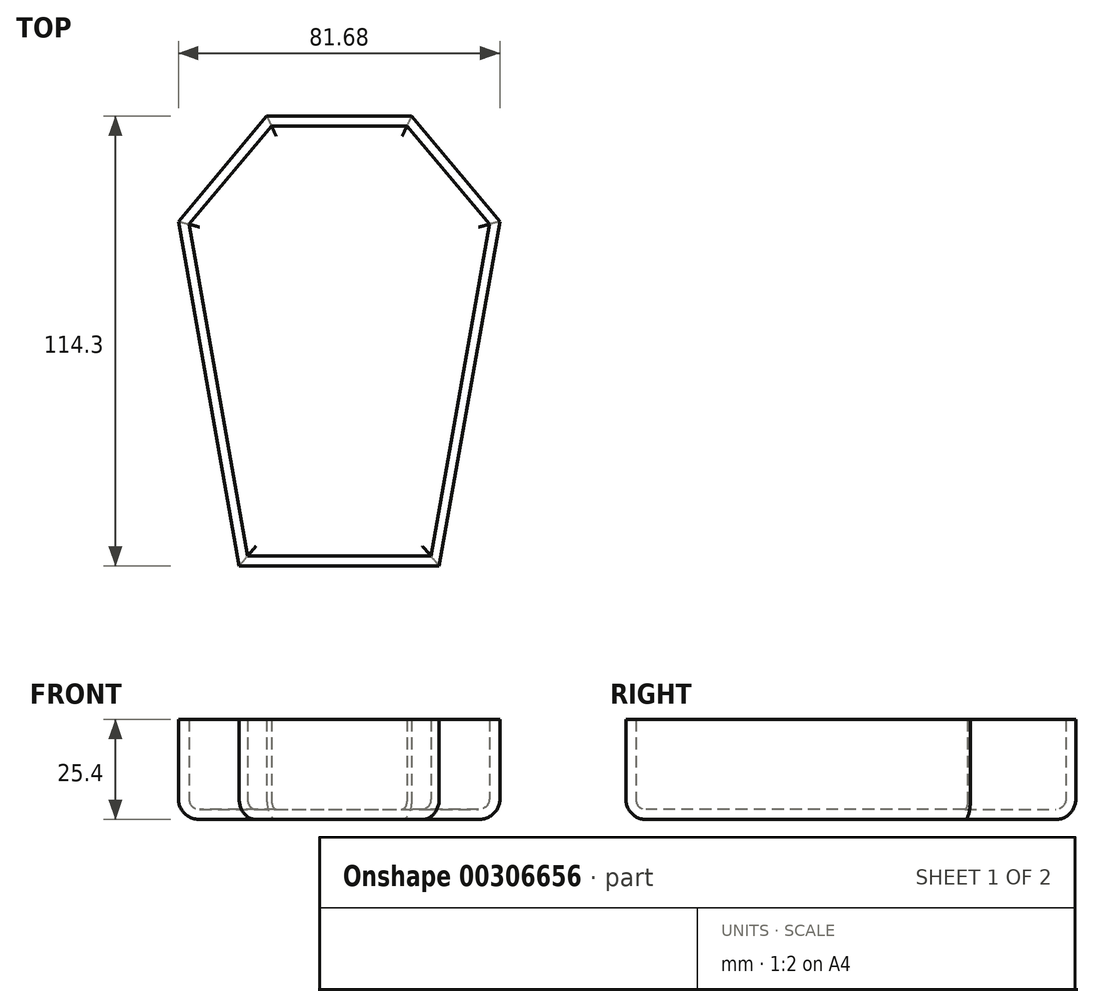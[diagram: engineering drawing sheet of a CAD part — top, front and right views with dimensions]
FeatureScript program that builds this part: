
annotation { "Feature Type Name" : "Feature", "Feature Type Description" : "" }
export const myFeature = defineFeature(function(context is Context, id is Id, definition is map)
    precondition{}
    {
        {
            var Q0;
            Q0=qCreatedBy(makeId("Top.planeOp"),FACE);
            var sketch = newSketch(context, id + "F0", { "sketchPlane" : qUnion([Q0])});
            skLineSegment(sketch, "E0", {"start": v(-35.6, 28) * mm, "end": v(-20.17, -59.55) * mm});
            skLineSegment(sketch, "E1", {"start": v(-20.17, -59.55) * mm, "end": v(30.63, -59.55) * mm});
            skLineSegment(sketch, "E2", {"start": v(30.63, -59.55) * mm, "end": v(46.07, 28) * mm});
            skLineSegment(sketch, "E3", {"start": v(46.07, 28) * mm, "end": v(23.62, 54.75) * mm});
            skLineSegment(sketch, "E4", {"start": v(23.62, 54.75) * mm, "end": v(-13.16, 54.75) * mm});
            skLineSegment(sketch, "E5", {"start": v(-13.16, 54.75) * mm, "end": v(-35.6, 28) * mm});
            skSolve(sketch);
        }
        {
            var Q0;
            Q0=makeQuery(id+"F0.imprint","IMPRINT",FACE,{"disambiguationData":[TD([[makeQuery(id+"F0.imprint","IMPRINT",EDGE,{"derivedFrom":sQuery(id+"F0.wireOp",EDGE,"E0")}),1.0]])]});
            extrude(context, id + "F1", {"entities" : qUnion([Q0]), "depth" : 25.4 * mm});
        }
        {
            var Q0;
            Q0=makeQuery(id+"F1.opExtrude","CAP_EDGE",EDGE,{"disambiguationData":[OSD([sQuery(id+"F0.wireOp",EDGE,"E0")])],"isStart":true});
            var Q1;
            Q1=makeQuery(id+"F1.opExtrude","CAP_EDGE",EDGE,{"disambiguationData":[OSD([sQuery(id+"F0.wireOp",EDGE,"E1")])],"isStart":true});
            var Q2;
            Q2=makeQuery(id+"F1.opExtrude","CAP_EDGE",EDGE,{"disambiguationData":[OSD([sQuery(id+"F0.wireOp",EDGE,"E2")])],"isStart":true});
            var Q3;
            Q3=makeQuery(id+"F1.opExtrude","CAP_EDGE",EDGE,{"disambiguationData":[OSD([sQuery(id+"F0.wireOp",EDGE,"E3")])],"isStart":true});
            var Q4;
            Q4=makeQuery(id+"F1.opExtrude","CAP_EDGE",EDGE,{"disambiguationData":[OSD([sQuery(id+"F0.wireOp",EDGE,"E4")])],"isStart":true});
            var Q5;
            Q5=makeQuery(id+"F1.opExtrude","CAP_EDGE",EDGE,{"disambiguationData":[OSD([sQuery(id+"F0.wireOp",EDGE,"E5")])],"isStart":true});
            fillet(context, id + "F2", {"entities" : qUnion([Q0, Q1, Q2, Q3, Q4, Q5]), "radius" : 5.08 * mm, "tangentPropagation" : true, "allowEdgeOverflow" : false});
        }
        {
            var Q0;
            Q0=makeQuery(id+"F1.opExtrude","CAP_FACE",FACE,{"disambiguationData":[OSD([sQuery(id+"F0.wireOp",EDGE,"E0"),sQuery(id+"F0.wireOp",EDGE,"E1"),sQuery(id+"F0.wireOp",EDGE,"E2"),sQuery(id+"F0.wireOp",EDGE,"E3"),sQuery(id+"F0.wireOp",EDGE,"E4"),sQuery(id+"F0.wireOp",EDGE,"E5")])],"isStart":false});
            shell(context, id + "F3", {"entities" : qUnion([Q0]), "thickness" : 2.54 * mm});
        }
    });
